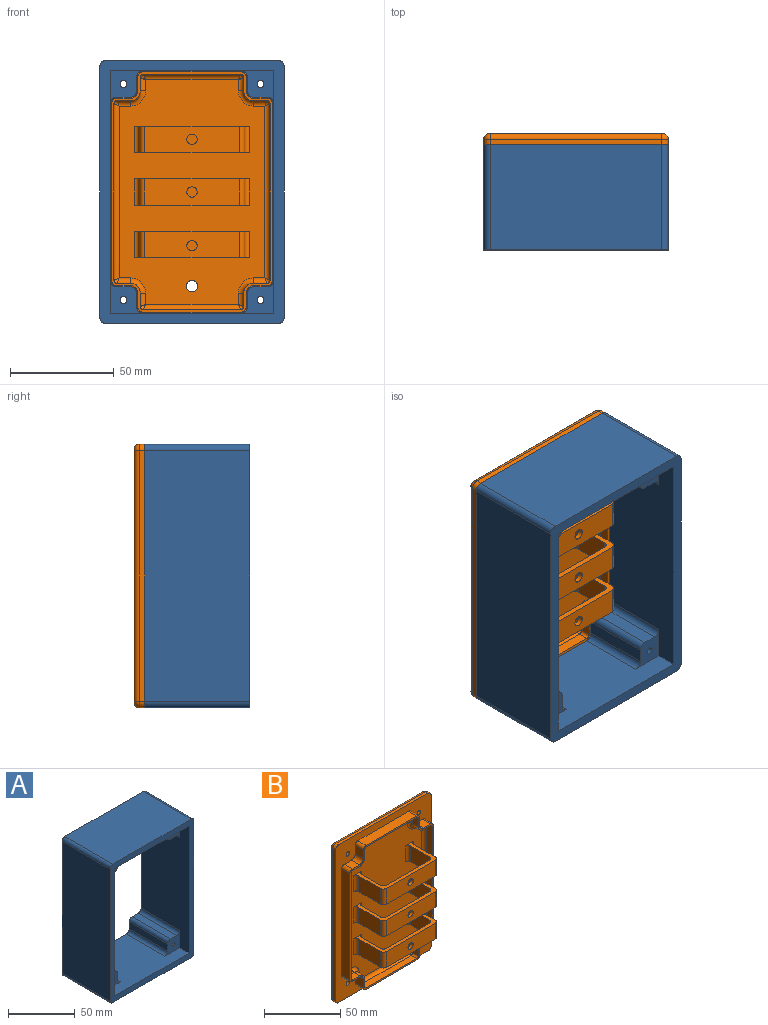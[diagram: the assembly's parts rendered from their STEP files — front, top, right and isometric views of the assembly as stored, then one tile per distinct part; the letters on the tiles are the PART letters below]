
ASSEMBLY  parts=2 mates=1
PART A: 42 faces, bbox 88.9x50.8x127 mm
  f0: plane 127x88.9mm, normal (0,-1,0), area 2082.6mm2, adj f1,f2,f3,f4,f7,f10,f13,f16
  f1: plane 121x50.8mm, normal (-1,0,0), area 6146.8mm2, adj f0,f17,f34,f37
  f2: plane 82.9x50.8mm, normal (0,0,-1), area 4211.3mm2, adj f0,f17,f34,f35
  f3: plane 121x50.8mm, normal (1,0,0), area 6146.8mm2, adj f0,f17,f35,f36
  f4: plane 78.74x50.8mm, normal (0,0,1), area 2718.9mm2, adj f0,f7,f13,f17,f19,f20,f26,f33
  f5: plane 40.8x6.7mm, normal (1,0,0), area 273.4mm2, adj f17,f20,f26,f41
  f6: plane 40.8x6.7mm, normal (0,0,1), area 273.4mm2, adj f17,f20,f27,f41
  f7: plane 116.84x50.8mm, normal (1,0,0), area 4654.4mm2, adj f0,f4,f10,f17,f18,f20,f27,f28
  f8: plane 40.8x6.7mm, normal (0,0,-1), area 273.4mm2, adj f17,f18,f28,f39
  f9: plane 40.8x6.7mm, normal (1,0,0), area 273.4mm2, adj f17,f18,f29,f39
  f10: plane 78.74x50.8mm, normal (0,0,-1), area 2718.9mm2, adj f0,f7,f13,f17,f18,f21,f29,f30
  f11: plane 40.8x6.7mm, normal (-1,0,0), area 273.4mm2, adj f17,f21,f30,f38
  f12: plane 40.8x6.7mm, normal (0,0,-1), area 273.4mm2, adj f17,f21,f31,f38
  f13: plane 116.84x50.8mm, normal (-1,0,0), area 4654.4mm2, adj f0,f4,f10,f17,f19,f21,f31,f32
  f14: plane 40.8x6.7mm, normal (0,0,1), area 273.4mm2, adj f17,f19,f32,f40
  f15: plane 40.8x6.7mm, normal (-1,0,0), area 273.4mm2, adj f17,f19,f33,f40
  f16: plane 82.9x50.8mm, normal (0,0,1), area 4211.3mm2, adj f0,f17,f36,f37
  f17: plane 127x88.9mm, normal (0,1,0), area 2701.3mm2, adj f1,f2,f3,f4,f5,f6,f7,f8
  f18: plane 15.7x15.7mm, normal (0,-1,0), area 154.7mm2, adj f7,f8,f9,f10,f23,f28,f29,f39
  f19: plane 15.7x15.7mm, normal (0,-1,0), area 154.7mm2, adj f4,f13,f14,f15,f25,f32,f33,f40
  f20: plane 15.7x15.7mm, normal (0,-1,0), area 154.7mm2, adj f4,f5,f6,f7,f24,f26,f27,f41
  f21: plane 15.7x15.7mm, normal (0,-1,0), area 154.7mm2, adj f10,f11,f12,f13,f22,f30,f31,f38
  f22: cylinder r=1.65mm len=40.8mm, axis (0,1,0), area 423mm2, adj f17,f21
  f23: cylinder r=1.65mm len=40.8mm, axis (0,1,0), area 423mm2, adj f17,f18
  f24: cylinder r=1.65mm len=40.8mm, axis (0,1,0), area 423mm2, adj f17,f20
  f25: cylinder r=1.65mm len=40.8mm, axis (0,1,0), area 423mm2, adj f17,f19
  f26: cylinder r=3mm len=40.8mm, axis (0,1,0), area 192.3mm2, adj f4,f5,f17,f20
  f27: cylinder r=3mm len=40.8mm, axis (0,1,0), area 192.3mm2, adj f6,f7,f17,f20
  f28: cylinder r=3mm len=40.8mm, axis (0,-1,0), area 192.3mm2, adj f7,f8,f17,f18
  f29: cylinder r=3mm len=40.8mm, axis (0,1,0), area 192.3mm2, adj f9,f10,f17,f18
  f30: cylinder r=3mm len=40.8mm, axis (0,-1,0), area 192.3mm2, adj f10,f11,f17,f21
  f31: cylinder r=3mm len=40.8mm, axis (0,-1,0), area 192.3mm2, adj f12,f13,f17,f21
  f32: cylinder r=3mm len=40.8mm, axis (0,1,0), area 192.3mm2, adj f13,f14,f17,f19
  f33: cylinder r=3mm len=40.8mm, axis (0,-1,0), area 192.3mm2, adj f4,f15,f17,f19
  f34: cylinder r=3mm len=50.8mm, axis (0,-1,0), area 239.4mm2, adj f0,f1,f2,f17
  f35: cylinder r=3mm len=50.8mm, axis (0,1,0), area 239.4mm2, adj f0,f2,f3,f17
  f36: cylinder r=3mm len=50.8mm, axis (0,-1,0), area 239.4mm2, adj f0,f3,f16,f17
  f37: cylinder r=3mm len=50.8mm, axis (0,1,0), area 239.4mm2, adj f0,f1,f16,f17
  f38: cylinder r=3mm len=40.8mm, axis (0,-1,0), area 192.3mm2, adj f11,f12,f17,f21
  f39: cylinder r=3mm len=40.8mm, axis (0,-1,0), area 192.3mm2, adj f8,f9,f17,f18
  f40: cylinder r=3mm len=40.8mm, axis (0,-1,0), area 192.3mm2, adj f14,f15,f17,f19
  f41: cylinder r=3mm len=40.8mm, axis (0,-1,0), area 192.3mm2, adj f5,f6,f17,f20
PART B: 148 faces, bbox 88.9x30.5x127 mm
  f0: plane 55.88x25.4mm, normal (0,0,-1), area 250.7mm2, adj f1,f70,f71,f73,f82,f83,f84,f99
  f1: plane 108.34x70.24mm, normal (0,-1,0), area 6406mm2, adj f0,f66,f68,f72,f75,f77,f93,f94
  f2: plane 127x88.9mm, normal (0,-1,0), area 2891.3mm2, adj f3,f4,f5,f6,f7,f8,f9,f10
  f3: plane 121x2.54mm, normal (1,0,0), area 307.3mm2, adj f2,f4,f14,f141
  f4: cylinder r=3mm len=3mm, axis (0,-1,0), area 12mm2, adj f2,f3,f5,f143
  f5: plane 82.9x2.54mm, normal (0,0,-1), area 210.6mm2, adj f2,f4,f6,f145
  f6: cylinder r=3mm len=3mm, axis (0,-1,0), area 12mm2, adj f2,f5,f7,f147
  f7: plane 121x2.54mm, normal (-1,0,0), area 307.3mm2, adj f2,f6,f8,f146
  f8: cylinder r=3mm len=3mm, axis (0,-1,0), area 12mm2, adj f2,f7,f9,f144
  f9: plane 82.9x2.54mm, normal (0,0,1), area 210.6mm2, adj f2,f8,f14,f142
  f10: cylinder r=1.65mm len=5.08mm, axis (0,-1,0), area 52.7mm2, adj f2,f15
  f11: cylinder r=1.65mm len=5.08mm, axis (0,-1,0), area 52.7mm2, adj f2,f15
  f12: cylinder r=1.65mm len=5.08mm, axis (0,-1,0), area 52.7mm2, adj f2,f15
  f13: cylinder r=1.65mm len=5.08mm, axis (0,-1,0), area 52.7mm2, adj f2,f15
  f14: cylinder r=3mm len=3mm, axis (0,-1,0), area 12mm2, adj f2,f3,f9,f140
  f15: plane 121.92x83.82mm, normal (0,1,0), area 10161.2mm2, adj f10,f11,f12,f13,f115,f140,f141,f142
  f16: cylinder r=3.51mm len=7.62mm, axis (0,1,0), area 42mm2, adj f2,f17,f55,f56
  f17: plane 7.62x6.7mm, normal (-1,0,0), area 51.1mm2, adj f2,f16,f18,f56
  f18: cylinder r=2.49mm len=7.62mm, axis (0,1,0), area 29.8mm2, adj f2,f17,f19,f56
  f19: plane 47.34x7.62mm, normal (0,0,1), area 360.7mm2, adj f2,f18,f20,f56
  f20: cylinder r=2.49mm len=7.62mm, axis (0,1,0), area 29.8mm2, adj f2,f19,f21,f56
  f21: plane 7.62x6.7mm, normal (1,0,0), area 51.1mm2, adj f2,f20,f22,f56
  f22: cylinder r=3.51mm len=7.62mm, axis (0,1,0), area 42mm2, adj f2,f21,f23,f56
  f23: plane 7.62x6.7mm, normal (0,0,1), area 51.1mm2, adj f2,f22,f24,f56
  f24: cylinder r=2.49mm len=7.62mm, axis (0,1,0), area 29.8mm2, adj f2,f23,f25,f56
  f25: plane 85.44x7.62mm, normal (1,0,0), area 651.1mm2, adj f2,f24,f26,f56
  f26: cylinder r=2.49mm len=7.62mm, axis (0,1,0), area 29.8mm2, adj f2,f25,f27,f56
  f27: plane 7.62x6.7mm, normal (0,0,-1), area 51.1mm2, adj f2,f26,f28,f56
  f28: cylinder r=3.51mm len=7.62mm, axis (0,1,0), area 42mm2, adj f2,f27,f29,f56
  f29: plane 7.62x6.7mm, normal (1,0,0), area 51.1mm2, adj f2,f28,f30,f56
  f30: cylinder r=2.49mm len=7.62mm, axis (0,1,0), area 29.8mm2, adj f2,f29,f31,f56
  f31: plane 47.34x7.62mm, normal (0,0,-1), area 360.7mm2, adj f2,f30,f32,f56
  f32: cylinder r=2.49mm len=7.62mm, axis (0,1,0), area 29.8mm2, adj f2,f31,f33,f56
  f33: plane 7.62x6.7mm, normal (-1,0,0), area 51.1mm2, adj f2,f32,f34,f56
  f34: cylinder r=3.51mm len=7.62mm, axis (0,1,0), area 42mm2, adj f2,f33,f35,f56
  f35: plane 7.62x6.7mm, normal (0,0,-1), area 51.1mm2, adj f2,f34,f36,f56
  f36: cylinder r=2.49mm len=7.62mm, axis (0,1,0), area 29.8mm2, adj f2,f35,f37,f56
  f37: plane 85.44x7.62mm, normal (-1,0,0), area 651.1mm2, adj f2,f36,f38,f56
  f38: cylinder r=2.49mm len=7.62mm, axis (0,1,0), area 29.8mm2, adj f2,f37,f55,f56
  f39: plane 6.49x5.08mm, normal (0,0,-1), area 33mm2, adj f54,f56,f57,f119
  f40: plane 85.02x5.08mm, normal (1,0,0), area 431.9mm2, adj f56,f57,f58,f116
  f41: plane 6.49x5.08mm, normal (0,0,1), area 33mm2, adj f42,f56,f58,f120
  f42: cylinder r=4.71mm len=5.08mm, axis (0,1,0), area 37.6mm2, adj f41,f43,f56,f122
  f43: plane 6.49x5.08mm, normal (1,0,0), area 33mm2, adj f42,f56,f59,f124
  f44: plane 46.92x5.08mm, normal (0,0,1), area 238.4mm2, adj f56,f59,f60,f128
  f45: plane 6.49x5.08mm, normal (-1,0,0), area 33mm2, adj f46,f56,f60,f132
  f46: cylinder r=4.71mm len=5.08mm, axis (0,1,0), area 37.6mm2, adj f45,f47,f56,f134
  f47: plane 6.49x5.08mm, normal (0,0,1), area 33mm2, adj f46,f56,f61,f136
  f48: plane 85.02x5.08mm, normal (-1,0,0), area 431.9mm2, adj f56,f61,f62,f139
  f49: plane 6.49x5.08mm, normal (0,0,-1), area 33mm2, adj f50,f56,f62,f135
  f50: cylinder r=4.71mm len=5.08mm, axis (0,1,0), area 37.6mm2, adj f49,f51,f56,f133
  f51: plane 6.49x5.08mm, normal (-1,0,0), area 33mm2, adj f50,f56,f63,f131
  f52: plane 46.92x5.08mm, normal (0,0,-1), area 238.4mm2, adj f56,f63,f64,f127
  f53: plane 6.49x5.08mm, normal (1,0,0), area 33mm2, adj f54,f56,f64,f123
  f54: cylinder r=4.71mm len=5.08mm, axis (0,1,0), area 37.6mm2, adj f39,f53,f56,f121
  f55: plane 7.62x6.7mm, normal (0,0,1), area 51.1mm2, adj f2,f16,f38,f56
  f56: plane 115.82x77.72mm, normal (0,-1,0), area 443.5mm2, adj f16,f17,f18,f19,f20,f21,f22,f23
  f57: cylinder r=1.5mm len=5.08mm, axis (0,1,0), area 12mm2, adj f39,f40,f56,f117
  f58: cylinder r=1.5mm len=5.08mm, axis (0,-1,0), area 12mm2, adj f40,f41,f56,f118
  f59: cylinder r=1.5mm len=5.08mm, axis (0,-1,0), area 12mm2, adj f43,f44,f56,f126
  f60: cylinder r=1.5mm len=5.08mm, axis (0,1,0), area 12mm2, adj f44,f45,f56,f130
  f61: cylinder r=1.5mm len=5.08mm, axis (0,-1,0), area 12mm2, adj f47,f48,f56,f138
  f62: cylinder r=1.5mm len=5.08mm, axis (0,1,0), area 12mm2, adj f48,f49,f56,f137
  f63: cylinder r=1.5mm len=5.08mm, axis (0,1,0), area 12mm2, adj f51,f52,f56,f129
  f64: cylinder r=1.5mm len=5.08mm, axis (0,-1,0), area 12mm2, adj f52,f53,f56,f125
  f65: plane 20.32x12.7mm, normal (-1,0,0), area 258.1mm2, adj f66,f68,f112,f114
  f66: plane 55.88x25.4mm, normal (0,0,-1), area 250.7mm2, adj f1,f65,f67,f69,f85,f86,f87,f91
  f67: plane 20.32x12.7mm, normal (1,0,0), area 258.1mm2, adj f66,f68,f111,f113
  f68: plane 55.88x25.4mm, normal (0,0,1), area 250.7mm2, adj f1,f65,f67,f69,f85,f86,f87,f91
  f69: plane 45.72x12.7mm, normal (0,-1,0), area 561mm2, adj f66,f68,f88,f113,f114
  f70: plane 20.32x12.7mm, normal (-1,0,0), area 258.1mm2, adj f0,f72,f104,f106
  f71: plane 20.32x12.7mm, normal (1,0,0), area 258.1mm2, adj f0,f72,f103,f105
  f72: plane 55.88x25.4mm, normal (0,0,1), area 250.7mm2, adj f1,f70,f71,f73,f82,f83,f84,f99
  f73: plane 45.72x12.7mm, normal (0,-1,0), area 561mm2, adj f0,f72,f90,f105,f106
  f74: plane 20.32x12.7mm, normal (-1,0,0), area 258.1mm2, adj f75,f77,f108,f110
  f75: plane 55.88x25.4mm, normal (0,0,-1), area 250.7mm2, adj f1,f74,f76,f78,f79,f80,f81,f92
  f76: plane 20.32x12.7mm, normal (1,0,0), area 258.1mm2, adj f75,f77,f107,f109
  f77: plane 55.88x25.4mm, normal (0,0,1), area 250.7mm2, adj f1,f74,f76,f78,f79,f80,f81,f92
  f78: plane 45.72x12.7mm, normal (0,-1,0), area 561mm2, adj f75,f77,f89,f109,f110
  f79: plane 17.78x12.7mm, normal (-1,0,0), area 225.8mm2, adj f75,f77,f92,f94
  f80: plane 17.78x12.7mm, normal (1,0,0), area 225.8mm2, adj f75,f77,f96,f98
  f81: plane 40.64x12.7mm, normal (0,1,0), area 496.5mm2, adj f75,f77,f89,f92,f98
  f82: plane 17.78x12.7mm, normal (1,0,0), area 225.8mm2, adj f0,f72,f101,f102
  f83: plane 17.78x12.7mm, normal (-1,0,0), area 225.8mm2, adj f0,f72,f99,f100
  f84: plane 40.64x12.7mm, normal (0,1,0), area 496.5mm2, adj f0,f72,f90,f99,f101
  f85: plane 40.64x12.7mm, normal (0,1,0), area 496.5mm2, adj f66,f68,f88,f91,f97
  f86: plane 17.78x12.7mm, normal (-1,0,0), area 225.8mm2, adj f66,f68,f91,f93
  f87: plane 17.78x12.7mm, normal (1,0,0), area 225.8mm2, adj f66,f68,f95,f97
  f88: cylinder r=2.5mm len=5mm, axis (0,-1,0), area 39.9mm2, adj f69,f85
  f89: cylinder r=2.5mm len=5mm, axis (0,-1,0), area 39.9mm2, adj f78,f81
  f90: cylinder r=2.5mm len=5mm, axis (0,-1,0), area 39.9mm2, adj f73,f84
  f91: cylinder r=2.54mm len=12.7mm, axis (0,0,-1), area 50.7mm2, adj f66,f68,f85,f86
  f92: cylinder r=2.54mm len=12.7mm, axis (0,0,-1), area 50.7mm2, adj f75,f77,f79,f81
  f93: cylinder r=2.54mm len=12.7mm, axis (0,0,-1), area 50.7mm2, adj f1,f66,f68,f86
  f94: cylinder r=2.54mm len=12.7mm, axis (0,0,-1), area 50.7mm2, adj f1,f75,f77,f79
  f95: cylinder r=2.54mm len=12.7mm, axis (0,0,-1), area 50.7mm2, adj f1,f66,f68,f87
  f96: cylinder r=2.54mm len=12.7mm, axis (0,0,-1), area 50.7mm2, adj f1,f75,f77,f80
  f97: cylinder r=2.54mm len=12.7mm, axis (0,0,-1), area 50.7mm2, adj f66,f68,f85,f87
  f98: cylinder r=2.54mm len=12.7mm, axis (0,0,-1), area 50.7mm2, adj f75,f77,f80,f81
  f99: cylinder r=2.54mm len=12.7mm, axis (0,0,-1), area 50.7mm2, adj f0,f72,f83,f84
  f100: cylinder r=2.54mm len=12.7mm, axis (0,0,-1), area 50.7mm2, adj f0,f1,f72,f83
  f101: cylinder r=2.54mm len=12.7mm, axis (0,0,-1), area 50.7mm2, adj f0,f72,f82,f84
  f102: cylinder r=2.54mm len=12.7mm, axis (0,0,-1), area 50.7mm2, adj f0,f1,f72,f82
  f103: cylinder r=2.54mm len=12.7mm, axis (0,0,-1), area 50.7mm2, adj f0,f1,f71,f72
  f104: cylinder r=2.54mm len=12.7mm, axis (0,0,1), area 50.7mm2, adj f0,f1,f70,f72
  f105: cylinder r=2.54mm len=12.7mm, axis (0,0,-1), area 50.7mm2, adj f0,f71,f72,f73
  f106: cylinder r=2.54mm len=12.7mm, axis (0,0,1), area 50.7mm2, adj f0,f70,f72,f73
  f107: cylinder r=2.54mm len=12.7mm, axis (0,0,-1), area 50.7mm2, adj f1,f75,f76,f77
  f108: cylinder r=2.54mm len=12.7mm, axis (0,0,1), area 50.7mm2, adj f1,f74,f75,f77
  f109: cylinder r=2.54mm len=12.7mm, axis (0,0,-1), area 50.7mm2, adj f75,f76,f77,f78
  f110: cylinder r=2.54mm len=12.7mm, axis (0,0,1), area 50.7mm2, adj f74,f75,f77,f78
  f111: cylinder r=2.54mm len=12.7mm, axis (0,0,-1), area 50.7mm2, adj f1,f66,f67,f68
  f112: cylinder r=2.54mm len=12.7mm, axis (0,0,1), area 50.7mm2, adj f1,f65,f66,f68
  f113: cylinder r=2.54mm len=12.7mm, axis (0,0,-1), area 50.7mm2, adj f66,f67,f68,f69
  f114: cylinder r=2.54mm len=12.7mm, axis (0,0,1), area 50.7mm2, adj f65,f66,f68,f69
  f115: cylinder r=2.75mm len=5.5mm, axis (0,-1,0), area 87.8mm2, adj f1,f15
  f116: cylinder r=2.54mm len=85.02mm, axis (0,0,-1), area 336.2mm2, adj f1,f40,f117,f118
  f117: bspline ~3.06x2.54mm, area 6.2mm2, adj f57,f116,f119
  f118: bspline ~3.06x2.54mm, area 6.2mm2, adj f58,f116,f120
  f119: cylinder r=2.54mm len=6.49mm, axis (-1,0,0), area 24.4mm2, adj f1,f39,f117,f121
  f120: cylinder r=2.54mm len=6.49mm, axis (1,0,0), area 24.4mm2, adj f1,f41,f118,f122
  f121: torus R=7.25mm, axis (0,1,0), area 35.3mm2, adj f1,f54,f119,f123
  f122: torus R=7.25mm, axis (0,1,0), area 35.3mm2, adj f1,f42,f120,f124
  f123: cylinder r=2.54mm len=6.49mm, axis (0,0,-1), area 24.4mm2, adj f1,f53,f121,f125
  f124: cylinder r=2.54mm len=6.49mm, axis (0,0,-1), area 24.4mm2, adj f1,f43,f122,f126
  f125: bspline ~3.06x2.54mm, area 6.2mm2, adj f64,f123,f127
  f126: bspline ~3.06x2.54mm, area 6.2mm2, adj f59,f124,f128
  f127: cylinder r=2.54mm len=46.92mm, axis (-1,0,0), area 184.2mm2, adj f1,f52,f125,f129
  f128: cylinder r=2.54mm len=46.92mm, axis (1,0,0), area 184.2mm2, adj f1,f44,f126,f130
  f129: bspline ~3.06x2.54mm, area 6.2mm2, adj f63,f127,f131
  f130: bspline ~3.06x2.54mm, area 6.2mm2, adj f60,f128,f132
  f131: cylinder r=2.54mm len=6.49mm, axis (0,0,1), area 24.4mm2, adj f1,f51,f129,f133
  f132: cylinder r=2.54mm len=6.49mm, axis (0,0,1), area 24.4mm2, adj f1,f45,f130,f134
  f133: torus R=7.25mm, axis (0,1,0), area 35.3mm2, adj f1,f50,f131,f135
  f134: torus R=7.25mm, axis (0,1,0), area 35.3mm2, adj f1,f46,f132,f136
  f135: cylinder r=2.54mm len=6.49mm, axis (-1,0,0), area 24.4mm2, adj f1,f49,f133,f137
  f136: cylinder r=2.54mm len=6.49mm, axis (1,0,0), area 24.4mm2, adj f1,f47,f134,f138
  f137: bspline ~3.06x2.54mm, area 6.2mm2, adj f62,f135,f139
  f138: bspline ~3.06x2.54mm, area 6.2mm2, adj f61,f136,f139
  f139: cylinder r=2.54mm len=85.02mm, axis (0,0,1), area 336.2mm2, adj f1,f48,f137,f138
  f140: torus R=0.46mm, axis (0,1,0), area 13mm2, adj f14,f15,f141,f142
  f141: cylinder r=2.54mm len=121mm, axis (0,0,1), area 482.8mm2, adj f3,f15,f140,f143
  f142: cylinder r=2.54mm len=82.9mm, axis (-1,0,0), area 330.8mm2, adj f9,f15,f140,f144
  f143: torus R=0.46mm, axis (0,1,0), area 13mm2, adj f4,f15,f141,f145
  f144: torus R=0.46mm, axis (0,1,0), area 13mm2, adj f8,f15,f142,f146
  f145: cylinder r=2.54mm len=82.9mm, axis (1,0,0), area 330.8mm2, adj f5,f15,f143,f147
  f146: cylinder r=2.54mm len=121mm, axis (0,0,-1), area 482.8mm2, adj f7,f15,f144,f147
  f147: torus R=0.46mm, axis (0,1,0), area 13mm2, adj f6,f15,f145,f146
PLACE A at identity
PLACE B t=(0,-84.33,0)mm
MATE fastened B.f10 <-> A.f22  axis (0,1,0) through (33.02,50.8,52.07)mm
